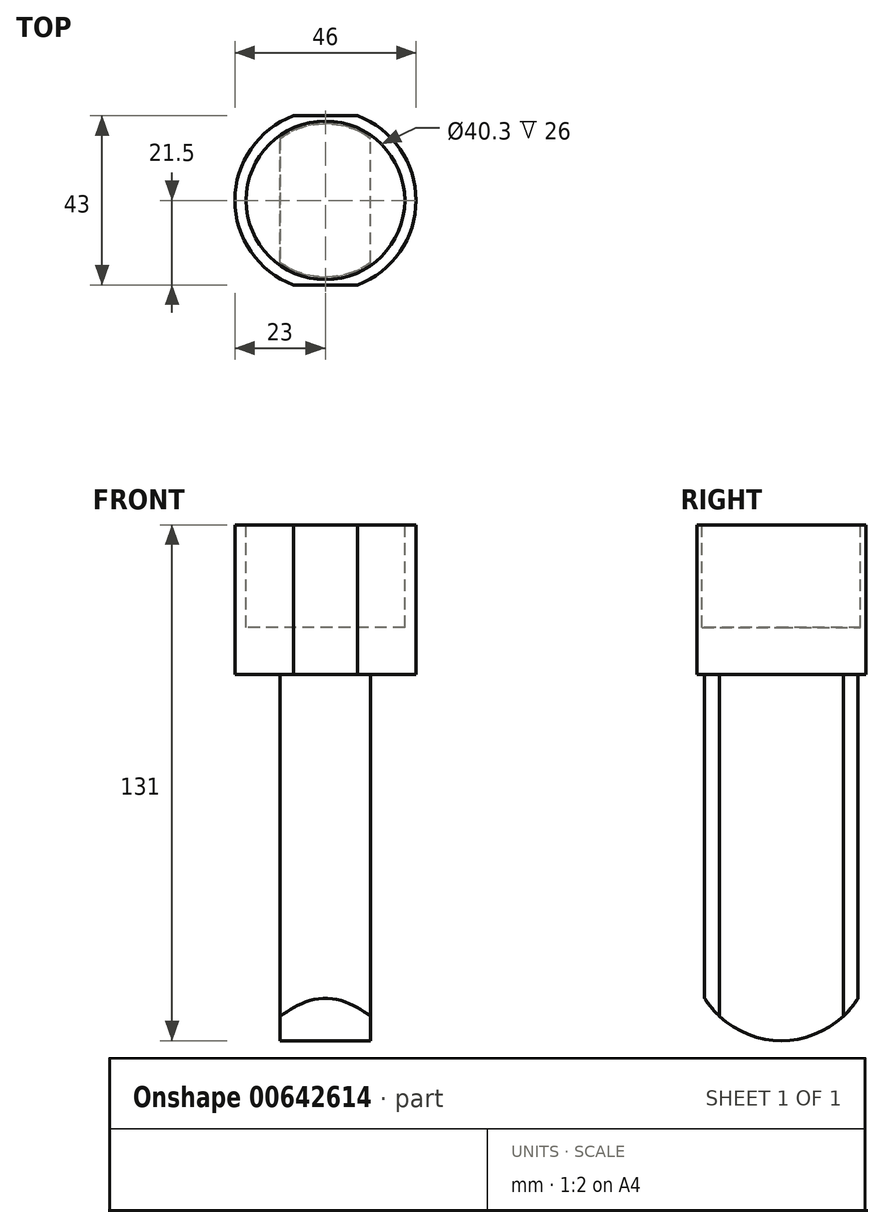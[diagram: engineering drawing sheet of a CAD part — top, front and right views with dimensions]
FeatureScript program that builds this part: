
annotation { "Feature Type Name" : "Feature", "Feature Type Description" : "" }
export const myFeature = defineFeature(function(context is Context, id is Id, definition is map)
    precondition{}
    {
        {
            var Q0;
            Q0=qCreatedBy(makeId("Top.planeOp"),FACE);
            var sketch = newSketch(context, id + "F0", { "sketchPlane" : qUnion([Q0])});
            skArc(sketch, "E0", {"start": v(8.17, -21.5) * mm, "mid": v(23, 0) * mm, "end": v(8.17, 21.5) * mm});
            skLineSegment(sketch, "E1", {"start": v(-8.17, -21.5) * mm, "end": v(8.17, -21.5) * mm});
            skLineSegment(sketch, "E2.MirrorCS", {"start": v(-8.17, 21.5) * mm, "end": v(8.17, 21.5) * mm});
            skArc(sketch, "E3.trimOffspring", {"start": v(-8.17, 21.5) * mm, "mid": v(-23, 0) * mm, "end": v(-8.17, -21.5) * mm});
            skSolve(sketch);
        }
        {
            var Q0;
            Q0=makeQuery(id+"F0.imprint","IMPRINT",FACE,{"disambiguationData":[TD([[makeQuery(id+"F0.imprint","IMPRINT",EDGE,{"derivedFrom":sQuery(id+"F0.wireOp",EDGE,"E0")}),1.0]])]});
            extrude(context, id + "F1", {"entities" : qUnion([Q0]), "depth" : 38 * mm, "offsetDistance" : 25 * mm});
        }
        {
            var Q0;
            Q0=makeQuery(id+"F1.opExtrude","CAP_FACE",FACE,{"disambiguationData":[OSD([sQuery(id+"F0.wireOp",EDGE,"E0"),sQuery(id+"F0.wireOp",EDGE,"E1"),sQuery(id+"F0.wireOp",EDGE,"E2.MirrorCS"),sQuery(id+"F0.wireOp",EDGE,"E3.trimOffspring")])],"isStart":false});
            var sketch = newSketch(context, id + "F2", { "sketchPlane" : qUnion([Q0])});
            skCircle(sketch, "E4", {"center": v(0, 0) * mm, "radius": 20.15 * mm});
            skSolve(sketch);
        }
        {
            var Q0;
            Q0 = qSketchRegion(id + "F2", true);
            extrude(context, id + "F3", {"entities" : qUnion([Q0]), "operationType" : NewBodyOperationType.REMOVE, "oppositeDirection" : true, "depth" : 26 * mm, "offsetDistance" : 25 * mm});
        }
        {
            var Q0;
            Q0=makeQuery(id+"F1.opExtrude","CAP_FACE",FACE,{"disambiguationData":[OSD([sQuery(id+"F0.wireOp",EDGE,"E0"),sQuery(id+"F0.wireOp",EDGE,"E1"),sQuery(id+"F0.wireOp",EDGE,"E2.MirrorCS"),sQuery(id+"F0.wireOp",EDGE,"E3.trimOffspring")])],"isStart":true});
            var sketch = newSketch(context, id + "F4", { "sketchPlane" : qUnion([Q0])});
            skArc(sketch, "E5", {"start": v(11.5, 15.75) * mm, "mid": v(0, 19.5) * mm, "end": v(-11.5, 15.75) * mm});
            skLineSegment(sketch, "E6", {"start": v(-11.5, 15.75) * mm, "end": v(-11.5, -15.75) * mm});
            skLineSegment(sketch, "E7.MirrorCS", {"start": v(11.5, 15.75) * mm, "end": v(11.5, -15.75) * mm});
            skArc(sketch, "E8.trimOffspring", {"start": v(-11.5, -15.75) * mm, "mid": v(0, -19.5) * mm, "end": v(11.5, -15.75) * mm});
            skSolve(sketch);
        }
        {
            var Q0;
            Q0=makeQuery(id+"F4.imprint","IMPRINT",FACE,{"disambiguationData":[TD([[makeQuery(id+"F4.imprint","IMPRINT",EDGE,{"derivedFrom":sQuery(id+"F4.wireOp",EDGE,"E5")}),1.0]])]});
            extrude(context, id + "F5", {"entities" : qUnion([Q0]), "operationType" : NewBodyOperationType.ADD, "depth" : 93 * mm, "offsetDistance" : 25 * mm});
        }
        {
            var Q0;
            Q0=makeQuery(id+"F5.opExtrude","SWEPT_FACE",FACE,{"disambiguationData":[OSD([sQuery(id+"F4.wireOp",EDGE,"E6")])]});
            var sketch = newSketch(context, id + "F6", { "sketchPlane" : qUnion([Q0])});
            skCircle(sketch, "E9", {"center": v(0, -70) * mm, "radius": 23 * mm});
            skLineSegment(sketch, "E10", {"start": v(-22.4, -75.26) * mm, "end": v(-30.58, -129.6) * mm});
            skLineSegment(sketch, "E11", {"start": v(-30.58, -129.6) * mm, "end": v(35.6, -133.6) * mm});
            skLineSegment(sketch, "E12", {"start": v(35.6, -133.6) * mm, "end": v(23, -69.36) * mm});
            skSolve(sketch);
        }
        {
            var Q0;
            {var subQ0=sQuery(id+"F6.wireOp",EDGE,"E10");Q0=makeQuery(id+"F6.imprint","IMPRINT",FACE,{"disambiguationData":[TD([[makeQuery(id+"F6.imprint","IMPRINT",EDGE,{"derivedFrom":subQ0}),1.0]])]});}
            var Q1;
            {var subQ0=sQuery(id+"F6.wireOp",EDGE,"E9");var subQ1=sQuery(id+"F4.wireOp",EDGE,"E6");var subQ4=makeQuery(id+"F5.opExtrude","CAP_EDGE",EDGE,{"disambiguationData":[OSD([subQ1])],"isStart":false});var subQ5=makeQuery(id+"F6.imprint","INTERSECT",VERTEX,{"derivedFrom":[subQ4,subQ0]});Q1=makeQuery(id+"F6.imprint","IMPRINT",FACE,{"disambiguationData":[TD([[makeQuery(id+"F6.imprint","IMPRINT",EDGE,{"disambiguationData":[TD([[subQ5,1.0]])],"derivedFrom":subQ0}),-1.0]])]});}
            var Q2;
            {var subQ0=sQuery(id+"F6.wireOp",EDGE,"E9");var subQ1=sQuery(id+"F4.wireOp",EDGE,"E6");var subQ2=makeQuery(id+"F5.opExtrude","CAP_EDGE",EDGE,{"disambiguationData":[OSD([subQ1])],"isStart":false});var subQ3=makeQuery(id+"F6.imprint","INTERSECT",VERTEX,{"derivedFrom":[subQ2,subQ0]});Q2=makeQuery(id+"F6.imprint","IMPRINT",FACE,{"disambiguationData":[TD([[makeQuery(id+"F6.imprint","IMPRINT",EDGE,{"disambiguationData":[TD([[subQ3,-1.0]])],"derivedFrom":subQ0}),-1.0]])]});}
            extrude(context, id + "F7", {"entities" : qUnion([Q0, Q1, Q2]), "operationType" : NewBodyOperationType.REMOVE, "endBound" : BoundingType.THROUGH_ALL, "oppositeDirection" : true, "depth" : 25 * mm, "offsetDistance" : 25 * mm});
        }
    });
